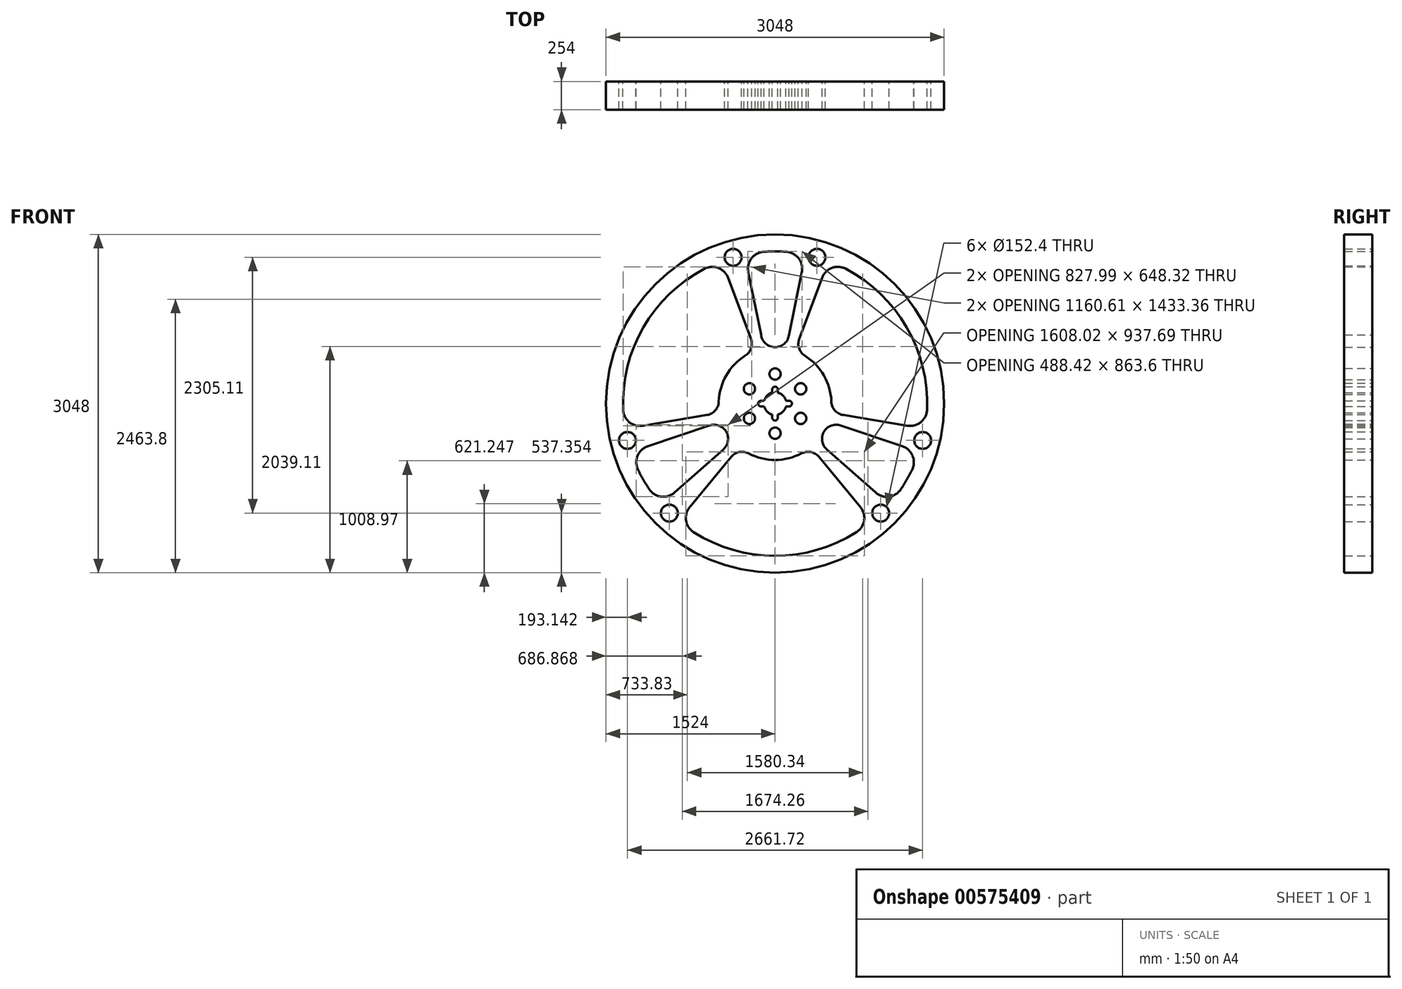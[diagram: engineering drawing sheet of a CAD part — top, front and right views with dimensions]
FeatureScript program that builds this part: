
annotation { "Feature Type Name" : "Feature", "Feature Type Description" : "" }
export const myFeature = defineFeature(function(context is Context, id is Id, definition is map)
    precondition{}
    {
        {
            var Q0;
            Q0=qCreatedBy(makeId("Front.planeOp"),FACE);
            var sketch = newSketch(context, id + "F0", { "sketchPlane" : qUnion([Q0])});
            skCircle(sketch, "E0", {"center": v(-378.06, 1318.47) * mm, "radius": 76.2 * mm});
            skCircle(sketch, "E1", {"center": v(378.06, 1318.47) * mm, "radius": 76.2 * mm});
            skCircle(sketch, "E2.1.0", {"center": v(-1330.86, -331.82) * mm, "radius": 76.2 * mm});
            skCircle(sketch, "E2.1.1", {"center": v(-952.8, -986.65) * mm, "radius": 76.2 * mm});
            skCircle(sketch, "E2.2.0", {"center": v(952.8, -986.65) * mm, "radius": 76.2 * mm});
            skCircle(sketch, "E2.2.1", {"center": v(1330.86, -331.82) * mm, "radius": 76.2 * mm});
            skArc(sketch, "E3", {"start": v(-269.48, 430.63) * mm, "mid": v(-439.94, 254) * mm, "end": v(-507.68, 18.06) * mm});
            skCircle(sketch, "E4", {"center": v(0, 0) * mm, "radius": 1524 * mm});
            skLineSegment(sketch, "E5", {"start": v(395.75, -480.08) * mm, "end": v(769.42, -933.39) * mm});
            skLineSegment(sketch, "E6", {"start": v(-395.75, -480.08) * mm, "end": v(-769.42, -933.39) * mm});
            skLineSegment(sketch, "E7", {"start": v(-465.98, -412.26) * mm, "end": v(-905.97, -801.53) * mm});
            skLineSegment(sketch, "E8", {"start": v(-590.02, -197.42) * mm, "end": v(-1147.13, -383.82) * mm});
            skLineSegment(sketch, "E9", {"start": v(-613.64, -102.69) * mm, "end": v(-1193.05, -199.64) * mm});
            skLineSegment(sketch, "E10", {"start": v(465.98, -412.26) * mm, "end": v(905.97, -801.53) * mm});
            skLineSegment(sketch, "E11", {"start": v(590.02, -197.42) * mm, "end": v(1147.13, -383.82) * mm});
            skLineSegment(sketch, "E12", {"start": v(613.64, -102.69) * mm, "end": v(1193.05, -199.64) * mm});
            skLineSegment(sketch, "E13", {"start": v(122.04, 599.85) * mm, "end": v(241.16, 1185.35) * mm});
            skLineSegment(sketch, "E14", {"start": v(-122.04, 599.85) * mm, "end": v(-241.16, 1185.35) * mm});
            skLineSegment(sketch, "E15", {"start": v(-217.9, 582.77) * mm, "end": v(-423.63, 1133.03) * mm});
            skLineSegment(sketch, "E16", {"start": v(217.9, 582.77) * mm, "end": v(423.63, 1133.03) * mm});
            skArc(sketch, "E17.trimOffspring", {"start": v(507.68, 18.06) * mm, "mid": v(439.94, 254) * mm, "end": v(269.48, 430.63) * mm});
            skArc(sketch, "E18.trimOffspring", {"start": v(-238.2, -448.7) * mm, "mid": v(0, -508) * mm, "end": v(238.2, -448.7) * mm});
            skArc(sketch, "E19.trimOffspring", {"start": v(-1236.12, -594.39) * mm, "mid": v(-1187.84, -685.8) * mm, "end": v(-1132.82, -773.3) * mm});
            skArc(sketch, "E20.trimOffspring", {"start": v(-733.3, -1159.11) * mm, "mid": v(0, -1371.6) * mm, "end": v(733.3, -1159.11) * mm});
            skArc(sketch, "E21.trimOffspring", {"start": v(1132.82, -773.3) * mm, "mid": v(1187.84, -685.8) * mm, "end": v(1236.12, -594.39) * mm});
            skArc(sketch, "E22.trimOffspring", {"start": v(1370.48, -55.5) * mm, "mid": v(1187.84, 685.8) * mm, "end": v(637.17, 1214.62) * mm});
            skArc(sketch, "E23.trimOffspring", {"start": v(103.3, 1367.7) * mm, "mid": v(0, 1371.6) * mm, "end": v(-103.3, 1367.7) * mm});
            skArc(sketch, "E24.trimOffspring", {"start": v(-637.17, 1214.62) * mm, "mid": v(-1187.84, 685.8) * mm, "end": v(-1370.48, -55.5) * mm});
            skPoint(sketch, "E25.visualSharp", {"position": v(-273.45, 1344.07) * mm});
            skArc(sketch, "E25.filletArc", {"start": v(-103.3, 1367.7) * mm, "mid": v(-213.38, 1307.65) * mm, "end": v(-241.16, 1185.35) * mm});
            skPoint(sketch, "E26.visualSharp", {"position": v(273.45, 1344.07) * mm});
            skArc(sketch, "E26.filletArc", {"start": v(241.16, 1185.35) * mm, "mid": v(213.38, 1307.65) * mm, "end": v(103.3, 1367.7) * mm});
            skPoint(sketch, "E27.visualSharp", {"position": v(480.35, 1284.74) * mm});
            skArc(sketch, "E27.filletArc", {"start": v(637.17, 1214.62) * mm, "mid": v(511.99, 1222.02) * mm, "end": v(423.63, 1133.03) * mm});
            skPoint(sketch, "E28.visualSharp", {"position": v(1352.8, -226.37) * mm});
            skArc(sketch, "E28.filletArc", {"start": v(1193.05, -199.64) * mm, "mid": v(1314.3, -167.62) * mm, "end": v(1370.48, -55.5) * mm});
            skPoint(sketch, "E29.visualSharp", {"position": v(1300.72, -435.21) * mm});
            skArc(sketch, "E29.filletArc", {"start": v(1236.12, -594.39) * mm, "mid": v(1239.15, -469.02) * mm, "end": v(1147.13, -383.82) * mm});
            skPoint(sketch, "E30.visualSharp", {"position": v(1027.27, -908.85) * mm});
            skArc(sketch, "E30.filletArc", {"start": v(905.97, -801.53) * mm, "mid": v(1025.76, -838.62) * mm, "end": v(1132.82, -773.3) * mm});
            skPoint(sketch, "E31.visualSharp", {"position": v(872.44, -1058.36) * mm});
            skArc(sketch, "E31.filletArc", {"start": v(733.3, -1159.11) * mm, "mid": v(802.31, -1054.4) * mm, "end": v(769.42, -933.39) * mm});
            skPoint(sketch, "E32.visualSharp", {"position": v(-872.44, -1058.36) * mm});
            skArc(sketch, "E32.filletArc", {"start": v(-769.42, -933.39) * mm, "mid": v(-802.31, -1054.4) * mm, "end": v(-733.3, -1159.11) * mm});
            skPoint(sketch, "E33.visualSharp", {"position": v(-1027.27, -908.85) * mm});
            skArc(sketch, "E33.filletArc", {"start": v(-1132.82, -773.3) * mm, "mid": v(-1025.76, -838.62) * mm, "end": v(-905.97, -801.53) * mm});
            skPoint(sketch, "E34.visualSharp", {"position": v(-1300.72, -435.21) * mm});
            skArc(sketch, "E34.filletArc", {"start": v(-1147.13, -383.82) * mm, "mid": v(-1239.15, -469.02) * mm, "end": v(-1236.12, -594.39) * mm});
            skPoint(sketch, "E35.visualSharp", {"position": v(-1352.8, -226.37) * mm});
            skArc(sketch, "E35.filletArc", {"start": v(-1370.48, -55.5) * mm, "mid": v(-1314.3, -167.62) * mm, "end": v(-1193.05, -199.64) * mm});
            skPoint(sketch, "E36.visualSharp", {"position": v(-480.35, 1284.74) * mm});
            skArc(sketch, "E36.filletArc", {"start": v(-423.63, 1133.03) * mm, "mid": v(-511.99, 1222.02) * mm, "end": v(-637.17, 1214.62) * mm});
            skArc(sketch, "E37", {"start": v(217.9, 582.77) * mm, "mid": v(216.57, 497.5) * mm, "end": v(269.48, 430.63) * mm});
            skArc(sketch, "E38", {"start": v(507.68, 18.06) * mm, "mid": v(539.14, -61.2) * mm, "end": v(613.64, -102.69) * mm});
            skArc(sketch, "E39", {"start": v(-238.2, -448.7) * mm, "mid": v(-322.57, -436.31) * mm, "end": v(-395.75, -480.08) * mm});
            skArc(sketch, "E40", {"start": v(395.75, -480.08) * mm, "mid": v(322.57, -436.31) * mm, "end": v(238.2, -448.7) * mm});
            skArc(sketch, "E41", {"start": v(-613.64, -102.69) * mm, "mid": v(-539.14, -61.2) * mm, "end": v(-507.68, 18.06) * mm});
            skArc(sketch, "E42", {"start": v(-269.48, 430.63) * mm, "mid": v(-216.57, 497.5) * mm, "end": v(-217.9, 582.77) * mm});
            skArc(sketch, "E43", {"start": v(-126.07, 619.68) * mm, "mid": v(0, 508) * mm, "end": v(126.07, 619.68) * mm});
            skArc(sketch, "E44.filletArc", {"start": v(-439.78, -254.28) * mm, "mid": v(-504.77, -199.08) * mm, "end": v(-590.02, -197.42) * mm});
            skArc(sketch, "E45.filletArc", {"start": v(-465.98, -412.26) * mm, "mid": v(-424.8, -337.6) * mm, "end": v(-440.1, -253.71) * mm});
            skArc(sketch, "E46.filletArc", {"start": v(590.02, -197.42) * mm, "mid": v(504.77, -199.08) * mm, "end": v(439.78, -254.28) * mm});
            skArc(sketch, "E47.filletArc", {"start": v(440.1, -253.71) * mm, "mid": v(424.8, -337.6) * mm, "end": v(465.98, -412.26) * mm});
            skCircle(sketch, "E48", {"center": v(0, 0) * mm, "radius": 381 * mm});
            skArc(sketch, "E49", {"start": v(-25.4, 98.37) * mm, "mid": v(-71.84, 71.84) * mm, "end": v(-98.37, 25.4) * mm});
            skArc(sketch, "E50", {"start": v(25.4, 127) * mm, "mid": v(0, 152.4) * mm, "end": v(-25.4, 127) * mm});
            skArc(sketch, "E51.1.0", {"start": v(-127, 25.4) * mm, "mid": v(-152.4, 0) * mm, "end": v(-127, -25.4) * mm});
            skArc(sketch, "E51.2.0", {"start": v(-25.4, -127) * mm, "mid": v(0, -152.4) * mm, "end": v(25.4, -127) * mm});
            skArc(sketch, "E51.3.0", {"start": v(127, -25.4) * mm, "mid": v(152.4, 0) * mm, "end": v(127, 25.4) * mm});
            skLineSegment(sketch, "E52", {"start": v(-25.4, 127) * mm, "end": v(-25.4, 98.37) * mm});
            skLineSegment(sketch, "E53", {"start": v(25.4, 127) * mm, "end": v(25.4, 98.37) * mm});
            skLineSegment(sketch, "E54", {"start": v(127, 25.4) * mm, "end": v(98.37, 25.4) * mm});
            skLineSegment(sketch, "E55", {"start": v(127, -25.4) * mm, "end": v(98.37, -25.4) * mm});
            skArc(sketch, "E56.trimOffspring", {"start": v(98.37, 25.4) * mm, "mid": v(71.84, 71.84) * mm, "end": v(25.4, 98.37) * mm});
            skLineSegment(sketch, "E57", {"start": v(-25.4, -127) * mm, "end": v(-25.4, -98.37) * mm});
            skLineSegment(sketch, "E58", {"start": v(25.4, -127) * mm, "end": v(25.4, -98.37) * mm});
            skArc(sketch, "E59.trimOffspring", {"start": v(25.4, -98.37) * mm, "mid": v(71.84, -71.84) * mm, "end": v(98.37, -25.4) * mm});
            skLineSegment(sketch, "E60", {"start": v(-127, 25.4) * mm, "end": v(-98.37, 25.4) * mm});
            skLineSegment(sketch, "E61", {"start": v(-127, -25.4) * mm, "end": v(-98.37, -25.4) * mm});
            skArc(sketch, "E62.trimOffspring", {"start": v(-98.37, -25.4) * mm, "mid": v(-71.84, -71.84) * mm, "end": v(-25.4, -98.37) * mm});
            skCircle(sketch, "E63", {"center": v(0, 266.7) * mm, "radius": 50.8 * mm});
            skCircle(sketch, "E64.1.0", {"center": v(-230.97, 133.35) * mm, "radius": 50.8 * mm});
            skCircle(sketch, "E64.2.0", {"center": v(-230.97, -133.35) * mm, "radius": 50.8 * mm});
            skCircle(sketch, "E64.3.0", {"center": v(0, -266.7) * mm, "radius": 50.8 * mm});
            skCircle(sketch, "E64.4.0", {"center": v(230.97, -133.35) * mm, "radius": 50.8 * mm});
            skCircle(sketch, "E64.5.0", {"center": v(230.97, 133.35) * mm, "radius": 50.8 * mm});
            skSolve(sketch);
        }
        {
            var Q0;
            Q0 = qSketchRegion(id + "F0", true);
            var Q1;
            Q1=makeQuery(id+"F0.imprint","IMPRINT",FACE,{"disambiguationData":[TD([[makeQuery(id+"F0.imprint","IMPRINT",EDGE,{"derivedFrom":sQuery(id+"F0.wireOp",EDGE,"E48")}),1.0]])]});
            extrude(context, id + "F1", {"entities" : qUnion([Q0, Q1]), "depth" : 254 * mm, "offsetDistance" : 25.4 * mm, "symmetric" : true});
        }
    });
